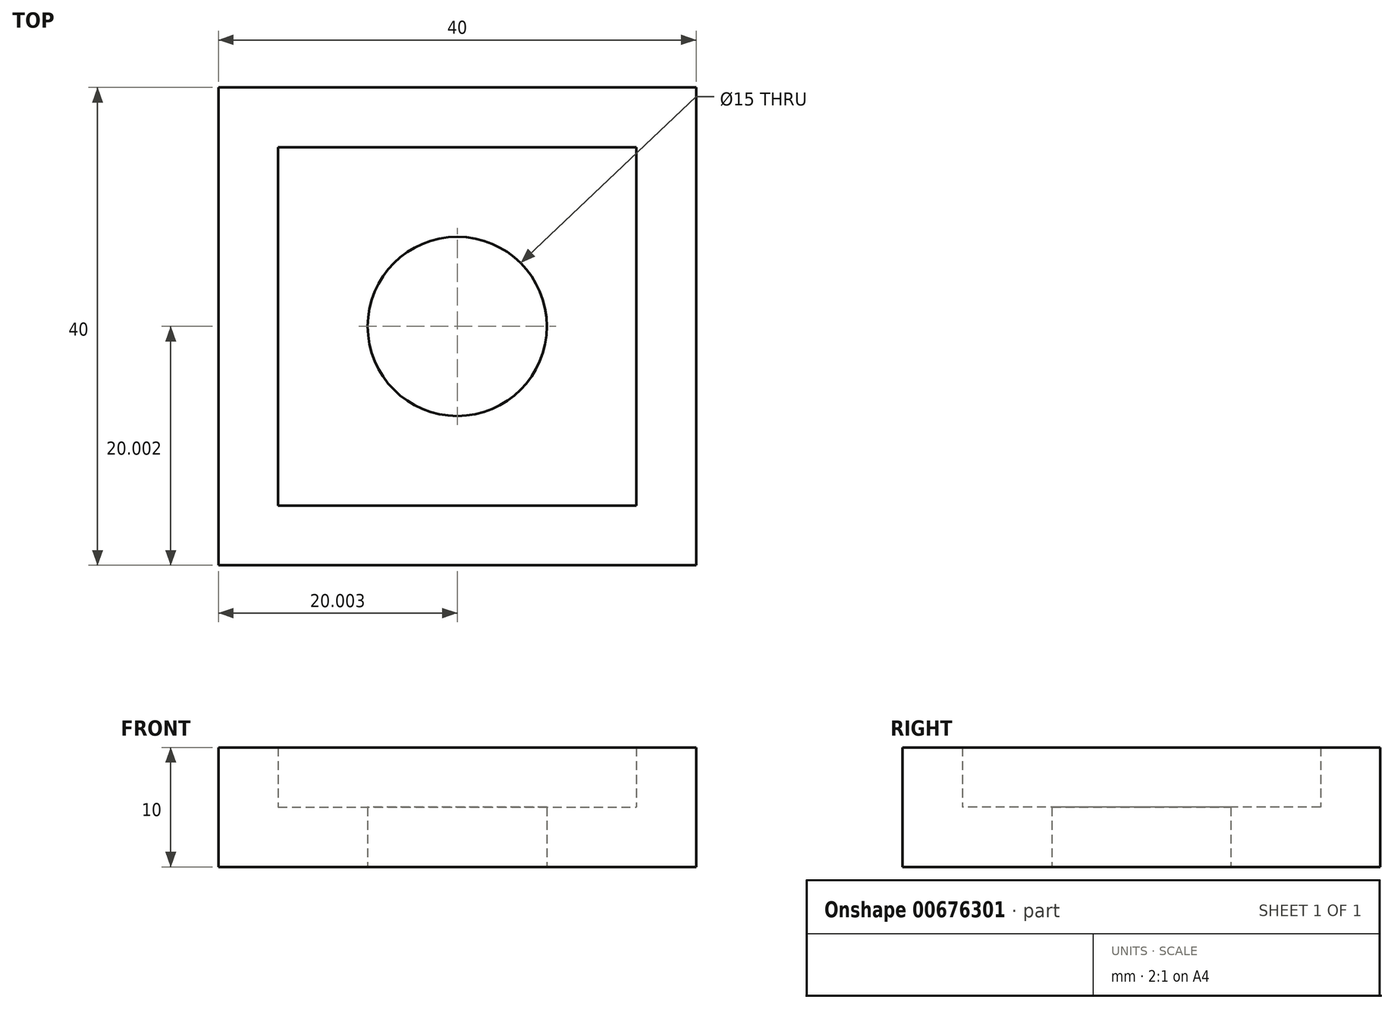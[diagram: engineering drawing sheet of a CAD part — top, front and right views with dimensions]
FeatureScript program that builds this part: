
annotation { "Feature Type Name" : "Feature", "Feature Type Description" : "" }
export const myFeature = defineFeature(function(context is Context, id is Id, definition is map)
    precondition{}
    {
        {
            var Q0;
            Q0=qCreatedBy(makeId("Top.planeOp"),FACE);
            var sketch = newSketch(context, id + "F0", { "sketchPlane" : qUnion([Q0])});
            skLineSegment(sketch, "E0.bottom", {"start": v(-19.98, 19.94) * mm, "end": v(20.02, 19.94) * mm});
            skLineSegment(sketch, "E0.top", {"start": v(-19.98, -20.06) * mm, "end": v(20.02, -20.06) * mm});
            skLineSegment(sketch, "E0.left", {"start": v(-19.98, 19.94) * mm, "end": v(-19.98, -20.06) * mm});
            skLineSegment(sketch, "E0.right", {"start": v(20.02, 19.94) * mm, "end": v(20.02, -20.06) * mm});
            skCircle(sketch, "E1", {"center": v(0.02, -0.06) * mm, "radius": 7.5 * mm});
            skLineSegment(sketch, "E2.bottom", {"start": v(-14.98, 14.94) * mm, "end": v(15.02, 14.94) * mm});
            skLineSegment(sketch, "E2.top", {"start": v(-14.98, -15.06) * mm, "end": v(15.02, -15.06) * mm});
            skLineSegment(sketch, "E2.left", {"start": v(-14.98, 14.94) * mm, "end": v(-14.98, -15.06) * mm});
            skLineSegment(sketch, "E2.right", {"start": v(15.02, 14.94) * mm, "end": v(15.02, -15.06) * mm});
            skSolve(sketch);
        }
        {
            var Q0;
            Q0=makeQuery(id+"F0.imprint","IMPRINT",FACE,{"disambiguationData":[TD([[makeQuery(id+"F0.imprint","IMPRINT",EDGE,{"derivedFrom":sQuery(id+"F0.wireOp",EDGE,"E1")}),-1.0]])]});
            extrude(context, id + "F1", {"entities" : qUnion([Q0]), "depth" : 5 * mm, "offsetDistance" : 25 * mm});
        }
        {
            var Q0;
            Q0 = qSketchRegion(id + "F0", true);
            extrude(context, id + "F2", {"entities" : qUnion([Q0]), "operationType" : NewBodyOperationType.ADD, "depth" : 10 * mm, "offsetDistance" : 25 * mm});
        }
    });
